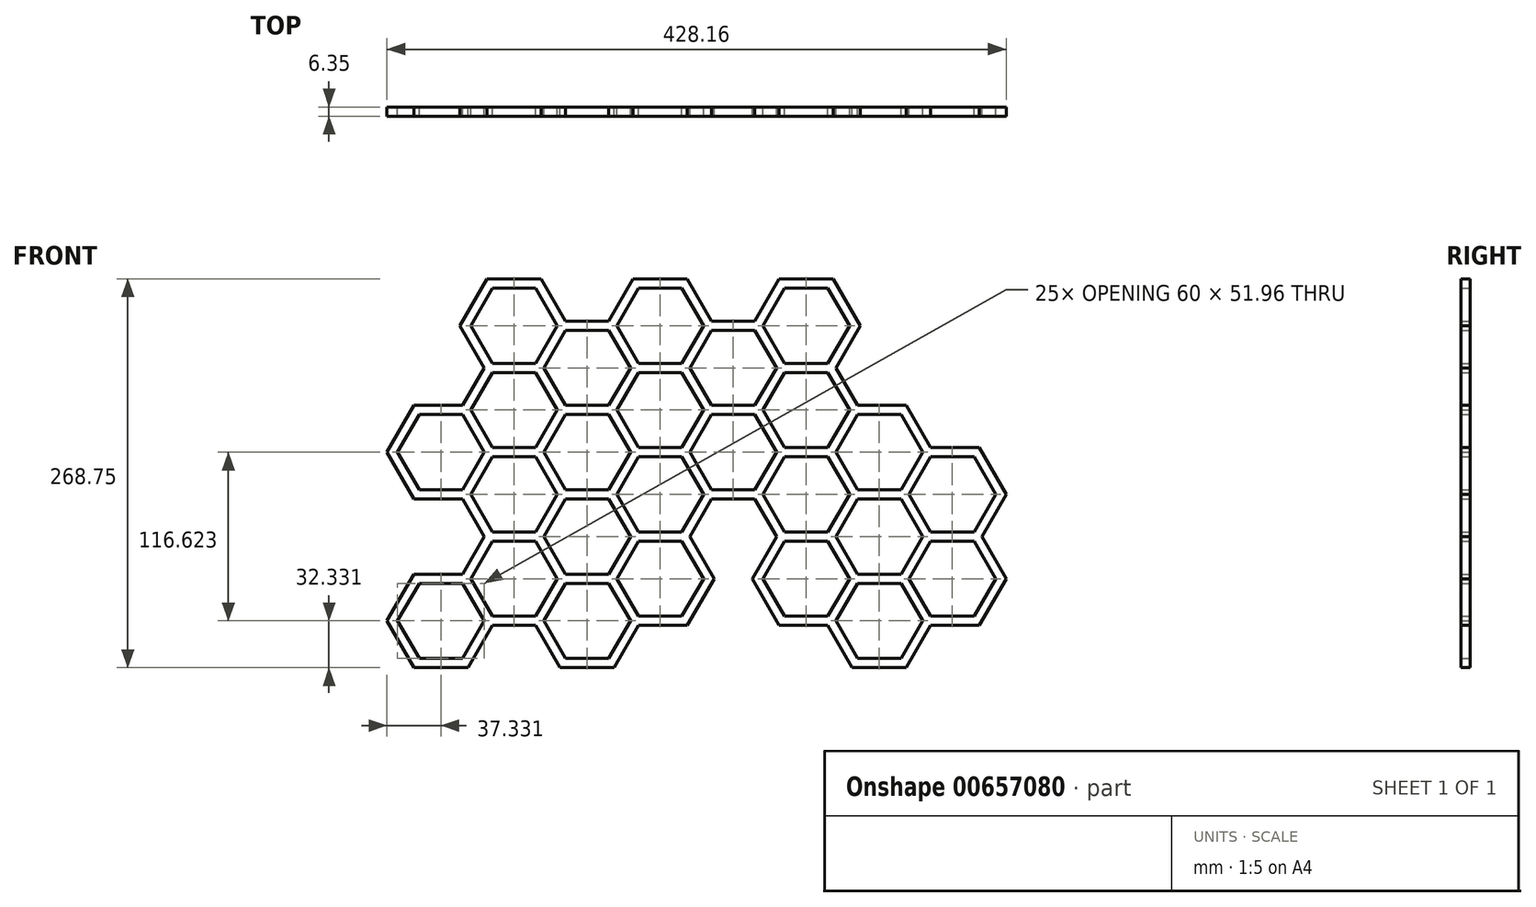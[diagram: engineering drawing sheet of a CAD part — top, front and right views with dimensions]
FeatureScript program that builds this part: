
annotation { "Feature Type Name" : "Feature", "Feature Type Description" : "" }
export const myFeature = defineFeature(function(context is Context, id is Id, definition is map)
    precondition{}
    {
        {
            var Q0;
            Q0=qCreatedBy(makeId("Front.planeOp"),FACE);
            var sketch = newSketch(context, id + "F0", { "sketchPlane" : qUnion([Q0])});
            skCircle(sketch, "E0.cCircle", {"center": v(-7.98, -23.48) * mm, "radius": 25.98 * mm, "construction": true});
            skLineSegment(sketch, "E0.0", {"start": v(22.02, -23.48) * mm, "end": v(7.02, -49.46) * mm});
            skLineSegment(sketch, "E0.1", {"start": v(7.02, -49.46) * mm, "end": v(-22.98, -49.46) * mm});
            skLineSegment(sketch, "E0.2", {"start": v(-22.98, -49.46) * mm, "end": v(-37.98, -23.48) * mm});
            skLineSegment(sketch, "E0.3", {"start": v(-37.98, -23.48) * mm, "end": v(-22.98, 2.5) * mm});
            skLineSegment(sketch, "E0.4", {"start": v(-22.98, 2.5) * mm, "end": v(7.02, 2.5) * mm});
            skLineSegment(sketch, "E0.5", {"start": v(7.02, 2.5) * mm, "end": v(22.02, -23.48) * mm});
            skPoint(sketch, "E0.0.midPoint", {"position": v(14.52, -36.47) * mm});
            skCircle(sketch, "E1.cCircle", {"center": v(-7.98, -81.8) * mm, "radius": 25.98 * mm, "construction": true});
            skLineSegment(sketch, "E1.0", {"start": v(22.02, -81.8) * mm, "end": v(7.02, -107.77) * mm});
            skLineSegment(sketch, "E1.1", {"start": v(7.02, -107.77) * mm, "end": v(-22.98, -107.77) * mm});
            skLineSegment(sketch, "E1.2", {"start": v(-22.98, -107.77) * mm, "end": v(-37.98, -81.8) * mm});
            skLineSegment(sketch, "E1.3", {"start": v(-37.98, -81.8) * mm, "end": v(-22.98, -55.81) * mm});
            skLineSegment(sketch, "E1.4", {"start": v(-22.98, -55.81) * mm, "end": v(7.02, -55.81) * mm});
            skLineSegment(sketch, "E1.5", {"start": v(7.02, -55.81) * mm, "end": v(22.02, -81.8) * mm});
            skPoint(sketch, "E1.0.midPoint", {"position": v(14.52, -94.78) * mm});
            skCircle(sketch, "E2.cCircle", {"center": v(-108.98, -81.8) * mm, "radius": 25.98 * mm, "construction": true});
            skLineSegment(sketch, "E2.0", {"start": v(-78.98, -81.8) * mm, "end": v(-93.98, -107.77) * mm});
            skLineSegment(sketch, "E2.1", {"start": v(-93.98, -107.77) * mm, "end": v(-123.98, -107.77) * mm});
            skLineSegment(sketch, "E2.2", {"start": v(-123.98, -107.77) * mm, "end": v(-138.98, -81.8) * mm});
            skLineSegment(sketch, "E2.3", {"start": v(-138.98, -81.8) * mm, "end": v(-123.98, -55.81) * mm});
            skLineSegment(sketch, "E2.4", {"start": v(-123.98, -55.81) * mm, "end": v(-93.98, -55.81) * mm});
            skLineSegment(sketch, "E2.5", {"start": v(-93.98, -55.81) * mm, "end": v(-78.98, -81.8) * mm});
            skPoint(sketch, "E2.0.midPoint", {"position": v(-86.48, -94.78) * mm});
            skCircle(sketch, "E3.cCircle", {"center": v(-108.98, -23.48) * mm, "radius": 25.98 * mm, "construction": true});
            skLineSegment(sketch, "E3.0", {"start": v(-78.98, -23.48) * mm, "end": v(-93.98, -49.46) * mm});
            skLineSegment(sketch, "E3.1", {"start": v(-93.98, -49.46) * mm, "end": v(-123.98, -49.46) * mm});
            skLineSegment(sketch, "E3.2", {"start": v(-123.98, -49.46) * mm, "end": v(-138.98, -23.48) * mm});
            skLineSegment(sketch, "E3.3", {"start": v(-138.98, -23.48) * mm, "end": v(-123.98, 2.5) * mm});
            skLineSegment(sketch, "E3.4", {"start": v(-123.98, 2.5) * mm, "end": v(-93.98, 2.5) * mm});
            skLineSegment(sketch, "E3.5", {"start": v(-93.98, 2.5) * mm, "end": v(-78.98, -23.48) * mm});
            skPoint(sketch, "E3.0.midPoint", {"position": v(-86.48, -36.47) * mm});
            skCircle(sketch, "E4.cCircle", {"center": v(-58.48, 5.67) * mm, "radius": 25.98 * mm, "construction": true});
            skLineSegment(sketch, "E4.0", {"start": v(-28.48, 5.67) * mm, "end": v(-43.48, -20.3) * mm});
            skLineSegment(sketch, "E4.1", {"start": v(-43.48, -20.3) * mm, "end": v(-73.48, -20.3) * mm});
            skLineSegment(sketch, "E4.2", {"start": v(-73.48, -20.3) * mm, "end": v(-88.48, 5.67) * mm});
            skLineSegment(sketch, "E4.3", {"start": v(-88.48, 5.67) * mm, "end": v(-73.48, 31.65) * mm});
            skLineSegment(sketch, "E4.4", {"start": v(-73.48, 31.65) * mm, "end": v(-43.48, 31.65) * mm});
            skLineSegment(sketch, "E4.5", {"start": v(-43.48, 31.65) * mm, "end": v(-28.48, 5.67) * mm});
            skPoint(sketch, "E4.0.midPoint", {"position": v(-35.98, -7.32) * mm});
            skCircle(sketch, "E5.cCircle", {"center": v(42.52, -110.95) * mm, "radius": 25.98 * mm, "construction": true});
            skLineSegment(sketch, "E5.0", {"start": v(72.52, -110.95) * mm, "end": v(57.52, -136.93) * mm});
            skLineSegment(sketch, "E5.1", {"start": v(57.52, -136.93) * mm, "end": v(27.52, -136.93) * mm});
            skLineSegment(sketch, "E5.2", {"start": v(27.52, -136.93) * mm, "end": v(12.52, -110.95) * mm});
            skLineSegment(sketch, "E5.3", {"start": v(12.52, -110.95) * mm, "end": v(27.52, -84.97) * mm});
            skLineSegment(sketch, "E5.4", {"start": v(27.52, -84.97) * mm, "end": v(57.52, -84.97) * mm});
            skLineSegment(sketch, "E5.5", {"start": v(57.52, -84.97) * mm, "end": v(72.52, -110.95) * mm});
            skPoint(sketch, "E5.0.midPoint", {"position": v(65.02, -123.94) * mm});
            skCircle(sketch, "E6.cCircle", {"center": v(-159.48, -110.95) * mm, "radius": 25.98 * mm, "construction": true});
            skLineSegment(sketch, "E6.0", {"start": v(-129.48, -110.95) * mm, "end": v(-144.48, -136.93) * mm});
            skLineSegment(sketch, "E6.1", {"start": v(-144.48, -136.93) * mm, "end": v(-174.48, -136.93) * mm});
            skLineSegment(sketch, "E6.2", {"start": v(-174.48, -136.93) * mm, "end": v(-189.48, -110.95) * mm});
            skLineSegment(sketch, "E6.3", {"start": v(-189.48, -110.95) * mm, "end": v(-174.48, -84.97) * mm});
            skLineSegment(sketch, "E6.4", {"start": v(-174.48, -84.97) * mm, "end": v(-144.48, -84.97) * mm});
            skLineSegment(sketch, "E6.5", {"start": v(-144.48, -84.97) * mm, "end": v(-129.48, -110.95) * mm});
            skPoint(sketch, "E6.0.midPoint", {"position": v(-136.98, -123.94) * mm});
            skCircle(sketch, "E7.cCircle", {"center": v(42.52, -52.64) * mm, "radius": 25.98 * mm, "construction": true});
            skLineSegment(sketch, "E7.0", {"start": v(72.52, -52.64) * mm, "end": v(57.52, -78.62) * mm});
            skLineSegment(sketch, "E7.1", {"start": v(57.52, -78.62) * mm, "end": v(27.52, -78.62) * mm});
            skLineSegment(sketch, "E7.2", {"start": v(27.52, -78.62) * mm, "end": v(12.52, -52.64) * mm});
            skLineSegment(sketch, "E7.3", {"start": v(12.52, -52.64) * mm, "end": v(27.52, -26.66) * mm});
            skLineSegment(sketch, "E7.4", {"start": v(27.52, -26.66) * mm, "end": v(57.52, -26.66) * mm});
            skLineSegment(sketch, "E7.5", {"start": v(57.52, -26.66) * mm, "end": v(72.52, -52.64) * mm});
            skPoint(sketch, "E7.0.midPoint", {"position": v(65.02, -65.63) * mm});
            skCircle(sketch, "E8.cCircle", {"center": v(93.02, -81.8) * mm, "radius": 25.98 * mm, "construction": true});
            skLineSegment(sketch, "E8.0", {"start": v(123.02, -81.8) * mm, "end": v(108.02, -107.77) * mm});
            skLineSegment(sketch, "E8.1", {"start": v(108.02, -107.77) * mm, "end": v(78.02, -107.77) * mm});
            skLineSegment(sketch, "E8.2", {"start": v(78.02, -107.77) * mm, "end": v(63.02, -81.8) * mm});
            skLineSegment(sketch, "E8.3", {"start": v(63.02, -81.8) * mm, "end": v(78.02, -55.81) * mm});
            skLineSegment(sketch, "E8.4", {"start": v(78.02, -55.81) * mm, "end": v(108.02, -55.81) * mm});
            skLineSegment(sketch, "E8.5", {"start": v(108.02, -55.81) * mm, "end": v(123.02, -81.8) * mm});
            skPoint(sketch, "E8.0.midPoint", {"position": v(115.52, -94.78) * mm});
            skCircle(sketch, "E9.cCircle", {"center": v(93.02, -23.48) * mm, "radius": 25.98 * mm, "construction": true});
            skLineSegment(sketch, "E9.0", {"start": v(123.02, -23.48) * mm, "end": v(108.02, -49.46) * mm});
            skLineSegment(sketch, "E9.1", {"start": v(108.02, -49.46) * mm, "end": v(78.02, -49.46) * mm});
            skLineSegment(sketch, "E9.2", {"start": v(78.02, -49.46) * mm, "end": v(63.02, -23.48) * mm});
            skLineSegment(sketch, "E9.3", {"start": v(63.02, -23.48) * mm, "end": v(78.02, 2.5) * mm});
            skLineSegment(sketch, "E9.4", {"start": v(78.02, 2.5) * mm, "end": v(108.02, 2.5) * mm});
            skLineSegment(sketch, "E9.5", {"start": v(108.02, 2.5) * mm, "end": v(123.02, -23.48) * mm});
            skPoint(sketch, "E9.0.midPoint", {"position": v(115.52, -36.47) * mm});
            skCircle(sketch, "E10.cCircle", {"center": v(42.52, 5.67) * mm, "radius": 25.98 * mm, "construction": true});
            skLineSegment(sketch, "E10.0", {"start": v(72.52, 5.67) * mm, "end": v(57.52, -20.3) * mm});
            skLineSegment(sketch, "E10.1", {"start": v(57.52, -20.3) * mm, "end": v(27.52, -20.3) * mm});
            skLineSegment(sketch, "E10.2", {"start": v(27.52, -20.3) * mm, "end": v(12.52, 5.67) * mm});
            skLineSegment(sketch, "E10.3", {"start": v(12.52, 5.67) * mm, "end": v(27.52, 31.65) * mm});
            skLineSegment(sketch, "E10.4", {"start": v(27.52, 31.65) * mm, "end": v(57.52, 31.65) * mm});
            skLineSegment(sketch, "E10.5", {"start": v(57.52, 31.65) * mm, "end": v(72.52, 5.67) * mm});
            skPoint(sketch, "E10.0.midPoint", {"position": v(65.02, -7.32) * mm});
            skCircle(sketch, "E11.cCircle", {"center": v(-7.98, 34.83) * mm, "radius": 25.98 * mm, "construction": true});
            skLineSegment(sketch, "E11.0", {"start": v(22.02, 34.83) * mm, "end": v(7.02, 8.85) * mm});
            skLineSegment(sketch, "E11.1", {"start": v(7.02, 8.85) * mm, "end": v(-22.98, 8.85) * mm});
            skLineSegment(sketch, "E11.2", {"start": v(-22.98, 8.85) * mm, "end": v(-37.98, 34.83) * mm});
            skLineSegment(sketch, "E11.3", {"start": v(-37.98, 34.83) * mm, "end": v(-22.98, 60.81) * mm});
            skLineSegment(sketch, "E11.4", {"start": v(-22.98, 60.81) * mm, "end": v(7.02, 60.81) * mm});
            skLineSegment(sketch, "E11.5", {"start": v(7.02, 60.81) * mm, "end": v(22.02, 34.83) * mm});
            skPoint(sketch, "E11.0.midPoint", {"position": v(14.52, 21.84) * mm});
            skCircle(sketch, "E12.cCircle", {"center": v(-7.98, 93.14) * mm, "radius": 25.98 * mm, "construction": true});
            skLineSegment(sketch, "E12.0", {"start": v(22.02, 93.14) * mm, "end": v(7.02, 67.16) * mm});
            skLineSegment(sketch, "E12.1", {"start": v(7.02, 67.16) * mm, "end": v(-22.98, 67.16) * mm});
            skLineSegment(sketch, "E12.2", {"start": v(-22.98, 67.16) * mm, "end": v(-37.98, 93.14) * mm});
            skLineSegment(sketch, "E12.3", {"start": v(-37.98, 93.14) * mm, "end": v(-22.98, 119.12) * mm});
            skLineSegment(sketch, "E12.4", {"start": v(-22.98, 119.12) * mm, "end": v(7.02, 119.12) * mm});
            skLineSegment(sketch, "E12.5", {"start": v(7.02, 119.12) * mm, "end": v(22.02, 93.14) * mm});
            skPoint(sketch, "E12.0.midPoint", {"position": v(14.52, 80.15) * mm});
            skCircle(sketch, "E13.cCircle", {"center": v(-58.48, 63.99) * mm, "radius": 25.98 * mm, "construction": true});
            skLineSegment(sketch, "E13.0", {"start": v(-28.48, 63.99) * mm, "end": v(-43.48, 38) * mm});
            skLineSegment(sketch, "E13.1", {"start": v(-43.48, 38) * mm, "end": v(-73.48, 38) * mm});
            skLineSegment(sketch, "E13.2", {"start": v(-73.48, 38) * mm, "end": v(-88.48, 63.99) * mm});
            skLineSegment(sketch, "E13.3", {"start": v(-88.48, 63.99) * mm, "end": v(-73.48, 89.97) * mm});
            skLineSegment(sketch, "E13.4", {"start": v(-73.48, 89.97) * mm, "end": v(-43.48, 89.97) * mm});
            skLineSegment(sketch, "E13.5", {"start": v(-43.48, 89.97) * mm, "end": v(-28.48, 63.99) * mm});
            skPoint(sketch, "E13.0.midPoint", {"position": v(-35.98, 51) * mm});
            skCircle(sketch, "E14.cCircle", {"center": v(-108.98, 34.83) * mm, "radius": 25.98 * mm, "construction": true});
            skLineSegment(sketch, "E14.0", {"start": v(-78.98, 34.83) * mm, "end": v(-93.98, 8.85) * mm});
            skLineSegment(sketch, "E14.1", {"start": v(-93.98, 8.85) * mm, "end": v(-123.98, 8.85) * mm});
            skLineSegment(sketch, "E14.2", {"start": v(-123.98, 8.85) * mm, "end": v(-138.98, 34.83) * mm});
            skLineSegment(sketch, "E14.3", {"start": v(-138.98, 34.83) * mm, "end": v(-123.98, 60.81) * mm});
            skLineSegment(sketch, "E14.4", {"start": v(-123.98, 60.81) * mm, "end": v(-93.98, 60.81) * mm});
            skLineSegment(sketch, "E14.5", {"start": v(-93.98, 60.81) * mm, "end": v(-78.98, 34.83) * mm});
            skPoint(sketch, "E14.0.midPoint", {"position": v(-86.48, 21.84) * mm});
            skCircle(sketch, "E15.cCircle", {"center": v(-108.98, 93.14) * mm, "radius": 25.98 * mm, "construction": true});
            skLineSegment(sketch, "E15.0", {"start": v(-78.98, 93.14) * mm, "end": v(-93.98, 67.16) * mm});
            skLineSegment(sketch, "E15.1", {"start": v(-93.98, 67.16) * mm, "end": v(-123.98, 67.16) * mm});
            skLineSegment(sketch, "E15.2", {"start": v(-123.98, 67.16) * mm, "end": v(-138.98, 93.14) * mm});
            skLineSegment(sketch, "E15.3", {"start": v(-138.98, 93.14) * mm, "end": v(-123.98, 119.12) * mm});
            skLineSegment(sketch, "E15.4", {"start": v(-123.98, 119.12) * mm, "end": v(-93.98, 119.12) * mm});
            skLineSegment(sketch, "E15.5", {"start": v(-93.98, 119.12) * mm, "end": v(-78.98, 93.14) * mm});
            skPoint(sketch, "E15.0.midPoint", {"position": v(-86.48, 80.15) * mm});
            skCircle(sketch, "E16.cCircle", {"center": v(-159.48, 63.99) * mm, "radius": 25.98 * mm, "construction": true});
            skLineSegment(sketch, "E16.0", {"start": v(-129.48, 63.99) * mm, "end": v(-144.48, 38) * mm});
            skLineSegment(sketch, "E16.1", {"start": v(-144.48, 38) * mm, "end": v(-174.48, 38) * mm});
            skLineSegment(sketch, "E16.2", {"start": v(-174.48, 38) * mm, "end": v(-189.48, 63.99) * mm});
            skLineSegment(sketch, "E16.3", {"start": v(-189.48, 63.99) * mm, "end": v(-174.48, 89.97) * mm});
            skLineSegment(sketch, "E16.4", {"start": v(-174.48, 89.97) * mm, "end": v(-144.48, 89.97) * mm});
            skLineSegment(sketch, "E16.5", {"start": v(-144.48, 89.97) * mm, "end": v(-129.48, 63.99) * mm});
            skPoint(sketch, "E16.0.midPoint", {"position": v(-136.98, 51) * mm});
            skCircle(sketch, "E17.cCircle", {"center": v(-159.48, 5.67) * mm, "radius": 25.98 * mm, "construction": true});
            skLineSegment(sketch, "E17.0", {"start": v(-129.48, 5.67) * mm, "end": v(-144.48, -20.3) * mm});
            skLineSegment(sketch, "E17.1", {"start": v(-144.48, -20.3) * mm, "end": v(-174.48, -20.3) * mm});
            skLineSegment(sketch, "E17.2", {"start": v(-174.48, -20.3) * mm, "end": v(-189.48, 5.67) * mm});
            skLineSegment(sketch, "E17.3", {"start": v(-189.48, 5.67) * mm, "end": v(-174.48, 31.65) * mm});
            skLineSegment(sketch, "E17.4", {"start": v(-174.48, 31.65) * mm, "end": v(-144.48, 31.65) * mm});
            skLineSegment(sketch, "E17.5", {"start": v(-144.48, 31.65) * mm, "end": v(-129.48, 5.67) * mm});
            skPoint(sketch, "E17.0.midPoint", {"position": v(-136.98, -7.32) * mm});
            skCircle(sketch, "E18.cCircle", {"center": v(-159.48, -52.64) * mm, "radius": 25.98 * mm, "construction": true});
            skLineSegment(sketch, "E18.0", {"start": v(-129.48, -52.64) * mm, "end": v(-144.48, -78.62) * mm});
            skLineSegment(sketch, "E18.1", {"start": v(-144.48, -78.62) * mm, "end": v(-174.48, -78.62) * mm});
            skLineSegment(sketch, "E18.2", {"start": v(-174.48, -78.62) * mm, "end": v(-189.48, -52.64) * mm});
            skLineSegment(sketch, "E18.3", {"start": v(-189.48, -52.64) * mm, "end": v(-174.48, -26.66) * mm});
            skLineSegment(sketch, "E18.4", {"start": v(-174.48, -26.66) * mm, "end": v(-144.48, -26.66) * mm});
            skLineSegment(sketch, "E18.5", {"start": v(-144.48, -26.66) * mm, "end": v(-129.48, -52.64) * mm});
            skPoint(sketch, "E18.0.midPoint", {"position": v(-136.98, -65.63) * mm});
            skCircle(sketch, "E19.cCircle", {"center": v(-209.98, -81.8) * mm, "radius": 25.98 * mm, "construction": true});
            skLineSegment(sketch, "E19.0", {"start": v(-179.98, -81.8) * mm, "end": v(-194.98, -107.77) * mm});
            skLineSegment(sketch, "E19.1", {"start": v(-194.98, -107.77) * mm, "end": v(-224.98, -107.77) * mm});
            skLineSegment(sketch, "E19.2", {"start": v(-224.98, -107.77) * mm, "end": v(-239.98, -81.8) * mm});
            skLineSegment(sketch, "E19.3", {"start": v(-239.98, -81.8) * mm, "end": v(-224.98, -55.81) * mm});
            skLineSegment(sketch, "E19.4", {"start": v(-224.98, -55.81) * mm, "end": v(-194.98, -55.81) * mm});
            skLineSegment(sketch, "E19.5", {"start": v(-194.98, -55.81) * mm, "end": v(-179.98, -81.8) * mm});
            skPoint(sketch, "E19.0.midPoint", {"position": v(-187.48, -94.78) * mm});
            skCircle(sketch, "E20.cCircle", {"center": v(-209.98, -23.48) * mm, "radius": 25.98 * mm, "construction": true});
            skLineSegment(sketch, "E20.0", {"start": v(-179.98, -23.48) * mm, "end": v(-194.98, -49.46) * mm});
            skLineSegment(sketch, "E20.1", {"start": v(-194.98, -49.46) * mm, "end": v(-224.98, -49.46) * mm});
            skLineSegment(sketch, "E20.2", {"start": v(-224.98, -49.46) * mm, "end": v(-239.98, -23.48) * mm});
            skLineSegment(sketch, "E20.3", {"start": v(-239.98, -23.48) * mm, "end": v(-224.98, 2.5) * mm});
            skLineSegment(sketch, "E20.4", {"start": v(-224.98, 2.5) * mm, "end": v(-194.98, 2.5) * mm});
            skLineSegment(sketch, "E20.5", {"start": v(-194.98, 2.5) * mm, "end": v(-179.98, -23.48) * mm});
            skPoint(sketch, "E20.0.midPoint", {"position": v(-187.48, -36.47) * mm});
            skCircle(sketch, "E21.cCircle", {"center": v(-209.98, 34.83) * mm, "radius": 25.98 * mm, "construction": true});
            skLineSegment(sketch, "E21.0", {"start": v(-179.98, 34.83) * mm, "end": v(-194.98, 8.85) * mm});
            skLineSegment(sketch, "E21.1", {"start": v(-194.98, 8.85) * mm, "end": v(-224.98, 8.85) * mm});
            skLineSegment(sketch, "E21.2", {"start": v(-224.98, 8.85) * mm, "end": v(-239.98, 34.83) * mm});
            skLineSegment(sketch, "E21.3", {"start": v(-239.98, 34.83) * mm, "end": v(-224.98, 60.81) * mm});
            skLineSegment(sketch, "E21.4", {"start": v(-224.98, 60.81) * mm, "end": v(-194.98, 60.81) * mm});
            skLineSegment(sketch, "E21.5", {"start": v(-194.98, 60.81) * mm, "end": v(-179.98, 34.83) * mm});
            skPoint(sketch, "E21.0.midPoint", {"position": v(-187.48, 21.84) * mm});
            skCircle(sketch, "E22.cCircle", {"center": v(-209.98, 93.14) * mm, "radius": 25.98 * mm, "construction": true});
            skLineSegment(sketch, "E22.0", {"start": v(-179.98, 93.14) * mm, "end": v(-194.98, 67.16) * mm});
            skLineSegment(sketch, "E22.1", {"start": v(-194.98, 67.16) * mm, "end": v(-224.98, 67.16) * mm});
            skLineSegment(sketch, "E22.2", {"start": v(-224.98, 67.16) * mm, "end": v(-239.98, 93.14) * mm});
            skLineSegment(sketch, "E22.3", {"start": v(-239.98, 93.14) * mm, "end": v(-224.98, 119.12) * mm});
            skLineSegment(sketch, "E22.4", {"start": v(-224.98, 119.12) * mm, "end": v(-194.98, 119.12) * mm});
            skLineSegment(sketch, "E22.5", {"start": v(-194.98, 119.12) * mm, "end": v(-179.98, 93.14) * mm});
            skPoint(sketch, "E22.0.midPoint", {"position": v(-187.48, 80.15) * mm});
            skCircle(sketch, "E23.cCircle", {"center": v(-260.48, 5.67) * mm, "radius": 25.98 * mm, "construction": true});
            skLineSegment(sketch, "E23.0", {"start": v(-230.48, 5.67) * mm, "end": v(-245.48, -20.3) * mm});
            skLineSegment(sketch, "E23.1", {"start": v(-245.48, -20.3) * mm, "end": v(-275.48, -20.3) * mm});
            skLineSegment(sketch, "E23.2", {"start": v(-275.48, -20.3) * mm, "end": v(-290.48, 5.67) * mm});
            skLineSegment(sketch, "E23.3", {"start": v(-290.48, 5.67) * mm, "end": v(-275.48, 31.65) * mm});
            skLineSegment(sketch, "E23.4", {"start": v(-275.48, 31.65) * mm, "end": v(-245.48, 31.65) * mm});
            skLineSegment(sketch, "E23.5", {"start": v(-245.48, 31.65) * mm, "end": v(-230.48, 5.67) * mm});
            skPoint(sketch, "E23.0.midPoint", {"position": v(-237.98, -7.32) * mm});
            skCircle(sketch, "E24.cCircle", {"center": v(-260.48, -110.95) * mm, "radius": 25.98 * mm, "construction": true});
            skLineSegment(sketch, "E24.0", {"start": v(-230.48, -110.95) * mm, "end": v(-245.48, -136.93) * mm});
            skLineSegment(sketch, "E24.1", {"start": v(-245.48, -136.93) * mm, "end": v(-275.48, -136.93) * mm});
            skLineSegment(sketch, "E24.2", {"start": v(-275.48, -136.93) * mm, "end": v(-290.48, -110.95) * mm});
            skLineSegment(sketch, "E24.3", {"start": v(-290.48, -110.95) * mm, "end": v(-275.48, -84.97) * mm});
            skLineSegment(sketch, "E24.4", {"start": v(-275.48, -84.97) * mm, "end": v(-245.48, -84.97) * mm});
            skLineSegment(sketch, "E24.5", {"start": v(-245.48, -84.97) * mm, "end": v(-230.48, -110.95) * mm});
            skPoint(sketch, "E24.0.midPoint", {"position": v(-237.98, -123.94) * mm});
            skLineSegment(sketch, "E25", {"start": v(-123.98, -114.12) * mm, "end": v(-140.81, -143.28) * mm});
            skLineSegment(sketch, "E26", {"start": v(-90.32, -114.12) * mm, "end": v(-71.65, -81.8) * mm});
            skLineSegment(sketch, "E27", {"start": v(-71.65, -81.8) * mm, "end": v(-88.48, -52.64) * mm});
            skLineSegment(sketch, "E28", {"start": v(-88.48, -52.64) * mm, "end": v(-73.48, -26.66) * mm});
            skLineSegment(sketch, "E29", {"start": v(-73.48, -26.66) * mm, "end": v(-43.48, -26.66) * mm});
            skLineSegment(sketch, "E30", {"start": v(-45.32, -81.8) * mm, "end": v(-26.65, -114.12) * mm});
            skLineSegment(sketch, "E31", {"start": v(-26.65, -114.12) * mm, "end": v(7.02, -114.12) * mm});
            skLineSegment(sketch, "E32", {"start": v(7.02, -114.12) * mm, "end": v(23.85, -143.28) * mm});
            skLineSegment(sketch, "E33", {"start": v(23.85, -143.28) * mm, "end": v(61.18, -143.28) * mm});
            skLineSegment(sketch, "E34", {"start": v(61.18, -143.28) * mm, "end": v(78.02, -114.12) * mm});
            skLineSegment(sketch, "E35", {"start": v(78.02, -114.12) * mm, "end": v(111.68, -114.12) * mm});
            skLineSegment(sketch, "E36", {"start": v(111.68, -114.12) * mm, "end": v(130.35, -81.8) * mm});
            skLineSegment(sketch, "E37", {"start": v(130.35, -81.8) * mm, "end": v(113.51, -52.64) * mm});
            skLineSegment(sketch, "E38", {"start": v(113.51, -52.64) * mm, "end": v(130.35, -23.48) * mm});
            skLineSegment(sketch, "E39", {"start": v(130.35, -23.48) * mm, "end": v(111.68, 8.85) * mm});
            skLineSegment(sketch, "E40", {"start": v(111.68, 8.85) * mm, "end": v(78.02, 8.85) * mm});
            skLineSegment(sketch, "E41", {"start": v(78.02, 8.85) * mm, "end": v(61.18, 38) * mm});
            skLineSegment(sketch, "E42", {"start": v(61.18, 38) * mm, "end": v(27.52, 38) * mm});
            skLineSegment(sketch, "E43", {"start": v(27.52, 38) * mm, "end": v(12.52, 63.99) * mm});
            skLineSegment(sketch, "E44", {"start": v(12.52, 63.99) * mm, "end": v(29.35, 93.14) * mm});
            skLineSegment(sketch, "E45", {"start": v(29.35, 93.14) * mm, "end": v(10.68, 125.47) * mm});
            skLineSegment(sketch, "E46", {"start": v(10.68, 125.47) * mm, "end": v(-26.65, 125.47) * mm});
            skLineSegment(sketch, "E47", {"start": v(-26.65, 125.47) * mm, "end": v(-43.48, 96.32) * mm});
            skLineSegment(sketch, "E48", {"start": v(-43.48, 96.32) * mm, "end": v(-73.48, 96.32) * mm});
            skLineSegment(sketch, "E49", {"start": v(-73.48, 96.32) * mm, "end": v(-90.32, 125.47) * mm});
            skLineSegment(sketch, "E50", {"start": v(-90.32, 125.47) * mm, "end": v(-127.65, 125.47) * mm});
            skLineSegment(sketch, "E51", {"start": v(-144.48, 96.32) * mm, "end": v(-127.65, 125.47) * mm});
            skLineSegment(sketch, "E52", {"start": v(-144.48, 96.32) * mm, "end": v(-174.48, 96.32) * mm});
            skLineSegment(sketch, "E53", {"start": v(-174.48, 96.32) * mm, "end": v(-191.31, 125.47) * mm});
            skLineSegment(sketch, "E54", {"start": v(-191.31, 125.47) * mm, "end": v(-228.65, 125.47) * mm});
            skLineSegment(sketch, "E55", {"start": v(-228.65, 125.47) * mm, "end": v(-247.31, 93.14) * mm});
            skLineSegment(sketch, "E56", {"start": v(-247.31, 93.14) * mm, "end": v(-230.48, 63.99) * mm});
            skLineSegment(sketch, "E57", {"start": v(-230.48, 63.99) * mm, "end": v(-245.48, 38) * mm});
            skLineSegment(sketch, "E58", {"start": v(-245.48, 38) * mm, "end": v(-279.15, 38) * mm});
            skLineSegment(sketch, "E59", {"start": v(-279.15, 38) * mm, "end": v(-297.81, 5.67) * mm});
            skLineSegment(sketch, "E60", {"start": v(-297.81, 5.67) * mm, "end": v(-279.15, -26.66) * mm});
            skLineSegment(sketch, "E61", {"start": v(-279.15, -26.66) * mm, "end": v(-245.48, -26.66) * mm});
            skLineSegment(sketch, "E62", {"start": v(-245.48, -26.66) * mm, "end": v(-230.48, -52.64) * mm});
            skLineSegment(sketch, "E63", {"start": v(-230.48, -52.64) * mm, "end": v(-245.48, -78.62) * mm});
            skLineSegment(sketch, "E64", {"start": v(-245.48, -78.62) * mm, "end": v(-279.15, -78.62) * mm});
            skLineSegment(sketch, "E65", {"start": v(-279.15, -78.62) * mm, "end": v(-297.81, -110.95) * mm});
            skLineSegment(sketch, "E66", {"start": v(-297.81, -110.95) * mm, "end": v(-279.15, -143.28) * mm});
            skLineSegment(sketch, "E67", {"start": v(-279.15, -143.28) * mm, "end": v(-241.81, -143.28) * mm});
            skLineSegment(sketch, "E68", {"start": v(-241.81, -143.28) * mm, "end": v(-224.98, -114.12) * mm});
            skLineSegment(sketch, "E69", {"start": v(-224.98, -114.12) * mm, "end": v(-194.98, -114.12) * mm});
            skLineSegment(sketch, "E70", {"start": v(-194.98, -114.12) * mm, "end": v(-178.15, -143.28) * mm});
            skLineSegment(sketch, "E71", {"start": v(-178.15, -143.28) * mm, "end": v(-140.81, -143.28) * mm});
            skLineSegment(sketch, "E72", {"start": v(-43.48, -26.66) * mm, "end": v(-28.48, -52.64) * mm});
            skLineSegment(sketch, "E73", {"start": v(-28.48, -52.64) * mm, "end": v(-45.32, -81.8) * mm});
            skLineSegment(sketch, "E74", {"start": v(-90.32, -114.12) * mm, "end": v(-123.98, -114.12) * mm});
            skSolve(sketch);
        }
        {
            var Q0;
            Q0 = qSketchRegion(id + "F0", true);
            extrude(context, id + "F1", {"entities" : qUnion([Q0]), "depth" : 6.35 * mm, "offsetDistance" : 25.4 * mm});
        }
    });
